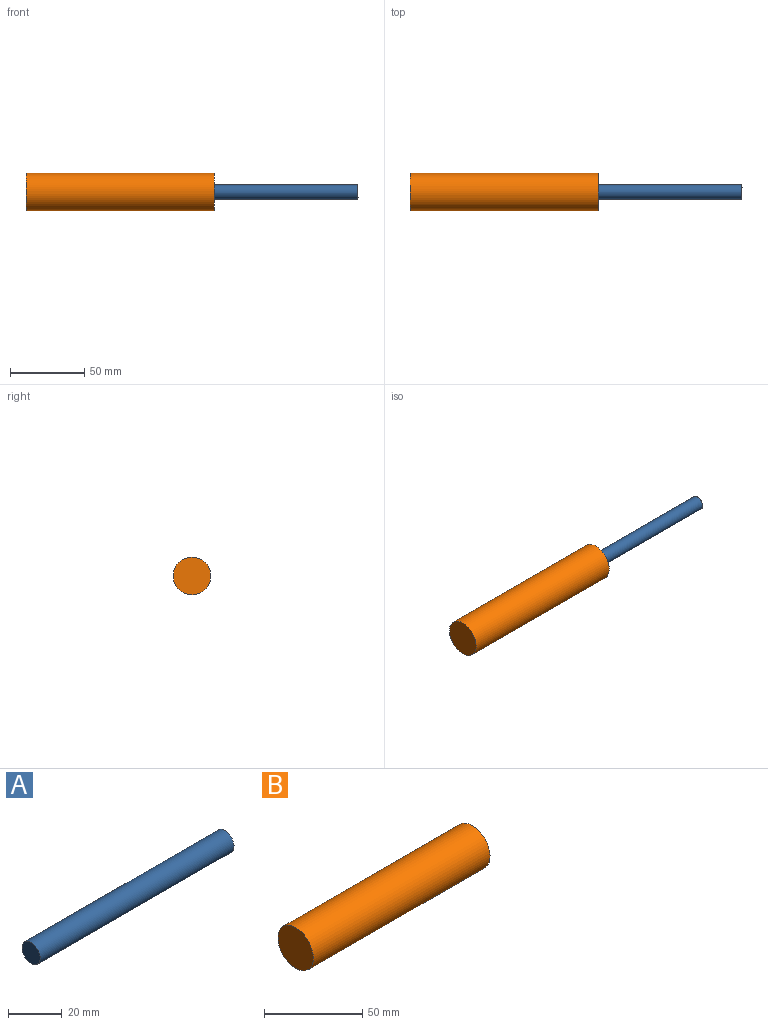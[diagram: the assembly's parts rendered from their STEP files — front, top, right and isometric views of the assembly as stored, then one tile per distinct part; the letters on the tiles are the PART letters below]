
ASSEMBLY  parts=2 mates=1
PART A: 3 faces, bbox 101.6x9.5x9.5 mm
  f0: cylinder r=4.76mm len=101.6mm, axis (-1,0,0), area 3040.2mm2, adj f1,f2
  f1: plane 9.53x9.53mm, normal (1,0,0), area 71.3mm2, adj f0
  f2: plane 9.53x9.53mm, normal (-1,0,0), area 71.3mm2, adj f0
PART B: 3 faces, bbox 127x25.4x25.4 mm
  f0: cylinder r=12.7mm len=127mm, axis (-1,0,0), area 10134.1mm2, adj f1,f2
  f1: plane 25.4x25.4mm, normal (1,0,0), area 506.7mm2, adj f0
  f2: plane 25.4x25.4mm, normal (-1,0,0), area 506.7mm2, adj f0
PLACE A rot(axis=(1,-0.03,-0.03),0deg) t=(-6.96,76.66,-50.97)mm
PLACE B rot(axis=(1,-0.03,-0.03),0deg) t=(-129.28,76.66,-50.97)mm
MATE slider B.f0 <-> A.f0  axis (1,0,0) through (-2.28,76.66,-50.97)mm
